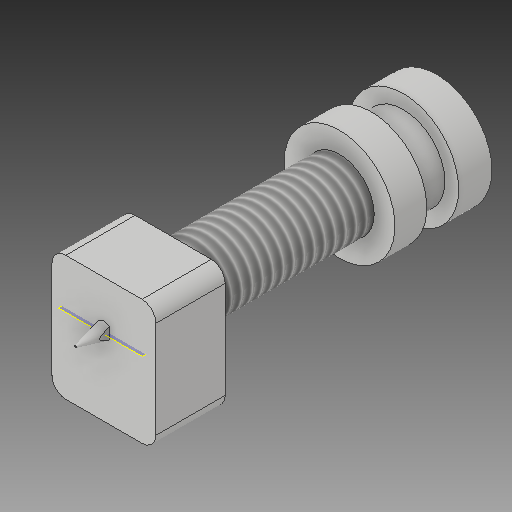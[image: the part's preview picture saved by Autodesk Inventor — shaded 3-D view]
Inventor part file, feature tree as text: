
AUTODESK INVENTOR PART (.ipt)
format: ipt  version: 2017 (Build 210142000, 142)  size: 186,880 bytes
history: native  units: mm
features: sketch x10, other x3, plane x1
ambient origin geometry x8: Origin, YZ Plane, XZ Plane, XY Plane, X Axis, Y Axis, Z Axis, Center Point
bodies: Solid1 (feature_tree)
feature tree (14):
  other  "Hotend Mock Up.ipt"
  other  "Solid1::Hotend Mock Up.ipt"
  other  "TaggingFeature1"
  sketch  "Sketch1"  dims[d0=10.0mm]
  sketch  "Sketch2"
  sketch  "Sketch3"
  sketch  "Sketch4"
  sketch  "Sketch5"
  sketch  "Sketch6"
  sketch  "Sketch7"
  sketch  "Sketch8"
  sketch  "Sketch9"
  sketch  "Sketch10"
  plane  "Work Plane1"
